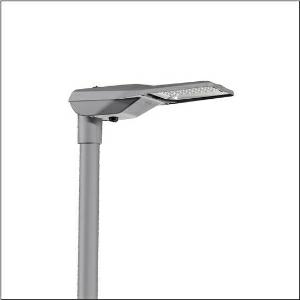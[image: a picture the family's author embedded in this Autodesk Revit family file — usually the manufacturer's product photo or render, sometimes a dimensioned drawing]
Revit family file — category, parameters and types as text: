
# Revit family: streetlight_sl_21_mini___p1_0a_5xe2a43t08hb_b918
name_source: partatom
category: Lighting Fixtures
units: mm (PartAtom-declared; Revit-internal decimal feet)

## family parameters
Cut with Voids When Loaded = No
Host = Face
Light Source = No
Part Type = Normal
Room Calculation Point = No
Round Connector Dimension = Use Diameter
Shared = No

## types (1)
- --- (1 x LED, 9430 lm, 66 W, 4000K)
    Apparent Load = 66 VA
    CIE Flux Codes = 21 50 90 100 100
    Color Rendering = 70
    Color Temperature = 4000K
    Default Elevation = 1800 mm
    Description = Streetlight SL 21 mini, mast luminaire, primary light control with lens, of PMMA, primary optical cover: cover, of toughened safety glass, transparent, light distribution: P1.0a, light emission: direct distribution, primary light characteristic: asymmetric, installation type: side-entry, post-top, LED, High Power LED, rated luminous flux: 9.430lm, luminous efficacy: 143lm/W, light colour: 740, colour temperature: 4000K, control gear: D4i, control: overheat protection, constant luminous flux control, time-dependent luminous flux control, flexible luminous flux parameterisation, pre-setting: logarithmic dimming characteristic, mains connection: 220..240V, AC, 50/60Hz, start of lifetime: 66W, end of service life: 69W, reduction: 30W, luminaire housing, of diecast aluminium, powder-coated, SITECO metallic grey (DB 702S), corrosivity category C5 high according to DIN EN ISO 12944, please order mast flange separately, inclination adjustable: 0°, 5°, 10°, 15°, sealing non-destructively replaceable, multi-level sealing system, length: 628mm, width: 235mm, height: 110mm, mast flange for spigot size: 42mm (side-entry): 5XC10008XM4, 60/48mm (side-entry/post-top): 5XC10108XM2, 76/60mm (side-entry/post-top): 5XC10108XM1, mounting height: 4..8m, Smart Interface below and above, protection rating (complete): IP66, insulation class (complete): insulation class II (safety insulation), certification: CE, ENEC, ENEC+, VDE, impact resistance: IK10, permissible operating ambient temperature for outdoor applications: -40..+50°C, standard-compliant lighting for roads and squares, packaging unit: 1 piece

Light Distribution: P1.0a
    Height = 110 mm
    Lamp = 1 x LED
    Lamp Light Flux = 9430 lm
    Lamp Power = 66 W
    Lamp count = 1
    Length = 625 mm
    Luminous efficacy = 143 lm/W
    Manufacturer = Siteco
    ModVariant = No
    Model = 5XE2A43T08HB
    Number of Poles = 1
    OnlyDefault = Yes
    Power Factor = 1
    Product Name = Streetlight SL 21 mini | P1.0a
    Product group = mast luminaire | pylon top
    ProductGroupID = 6100
    Protection Class = Protection class II
    Protection Degree = IP 66
    RLX_Detail_Level = 1
    RLX_Emergency_Light_Flux = 0 lm
    RLX_Emergency_Type = 0
    RLX_Emergency_Type_DB = No
    RlxData = <blob elided: 37477 chars, md5=90928b0c>
    Socket = socket
    Standby Power = 0 W
    System Light Flux = 9430 lm
    System Power = 66 W
    Type Comments = factory setting: luminous flux: 100 % | dim-lin: 254 | 670 mA
    Type Image = l_1003514.jpg
    URL = http://relux.com
    VarID = @adj_183907
    Voltage = 0 V
    Weight = 0.00 kg
    Width = 234 mm

## geometry (parser evidence)
native form markers: Blend x4, Sweep x10
no freeform markers — native parametric forms only
